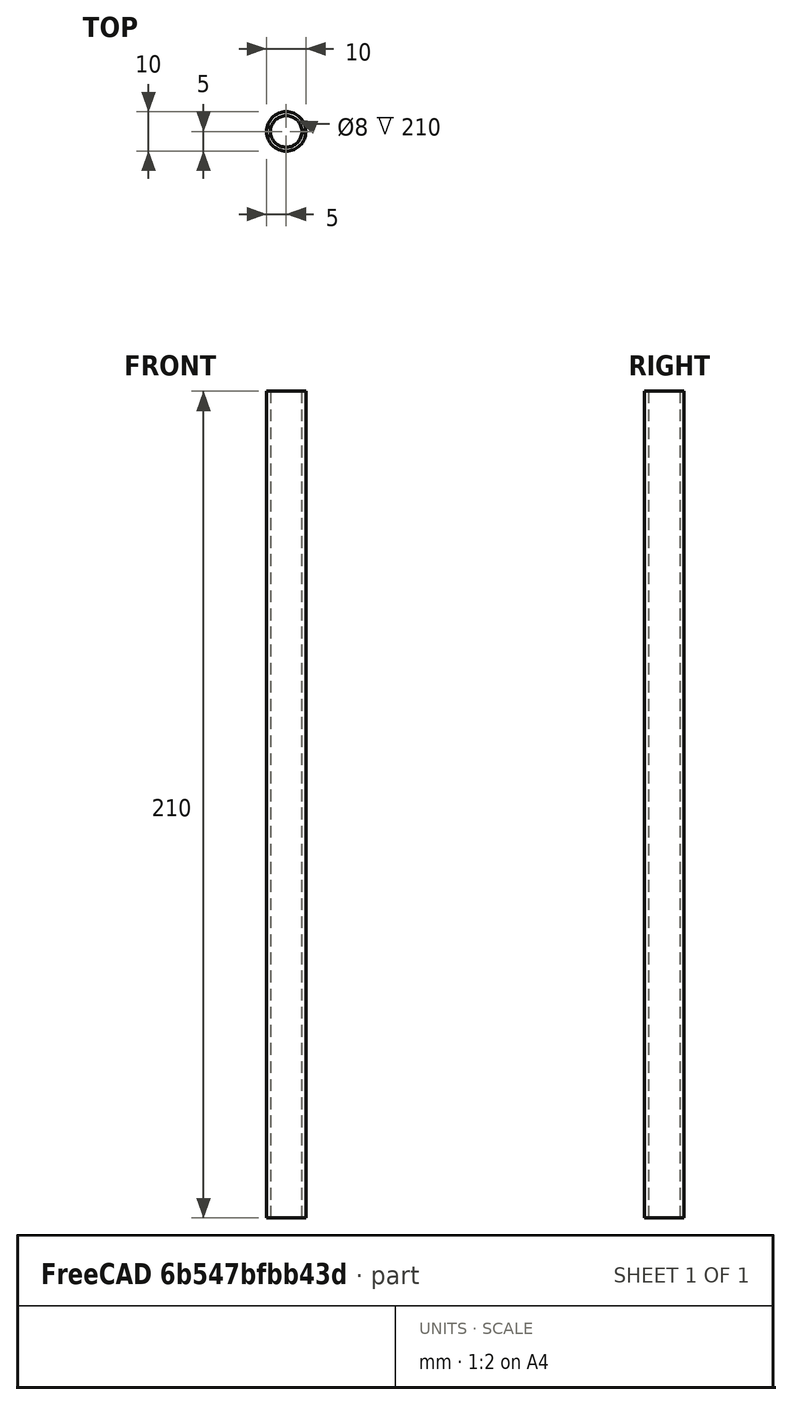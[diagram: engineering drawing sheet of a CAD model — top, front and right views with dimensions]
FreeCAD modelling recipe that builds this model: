
FCSTD DOCUMENT  (FreeCAD 0.19R24276 (Git))
Label: Tube_210_for_arm_250_back
License: All rights reserved
LicenseURL: http://en.wikipedia.org/wiki/All_rights_reserved
objects: Sketcher::SketchObject×1, PartDesign::Pad×1, PartDesign::Body×1
note: 4 computed .brp shape members not serialized (recipe doc carries the construction recipe); baked Part::Feature solids carry a one-line shape summary decoded from their .brp

FEATURE [Sketcher::SketchObject] Sketch
  FullyConstrained = true
  MapMode = 5
  Support = -> [XY_Plane]
  sketch-geometry (2):
    g0: Circle CenterX=0 CenterY=0 CenterZ=0 NormalX=0 NormalY=0 NormalZ=1 AngleXU=0 Radius=4
    g1: Circle CenterX=0 CenterY=0 CenterZ=0 NormalX=0 NormalY=0 NormalZ=1 AngleXU=0 Radius=5
  constraints (4):
    c: Coincident(g0,g-1)
    c: Coincident(g1,g0)
    c: Diameter(g0) = 8
    c: Diameter(g1) = 10
FEATURE [PartDesign::Pad] Pad
  Direction = (1,1,1)
  Length = 210
  Length2 = 100
  Profile = -> Sketch
  Type = 0
FEATURE [PartDesign::Body] Body
  Group = -> [Sketch,Pad]
  Origin = -> Origin
  Tip = -> Pad
